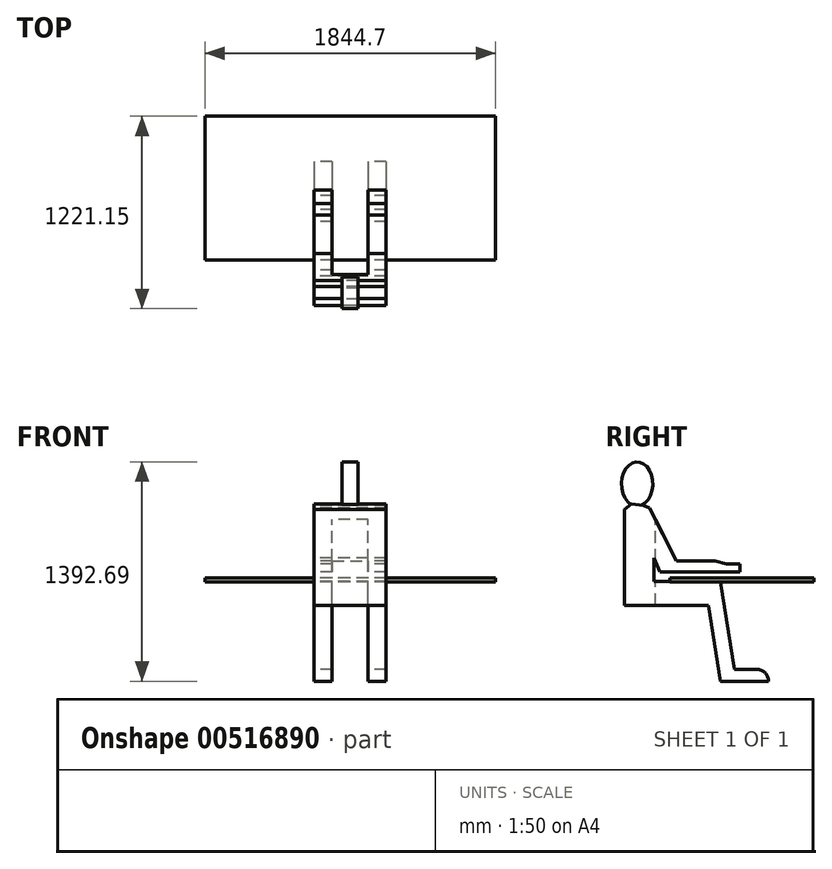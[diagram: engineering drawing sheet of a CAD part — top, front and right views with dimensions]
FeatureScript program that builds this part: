
annotation { "Feature Type Name" : "Feature", "Feature Type Description" : "" }
export const myFeature = defineFeature(function(context is Context, id is Id, definition is map)
    precondition{}
    {
        {
            var Q0;
            Q0=qCreatedBy(makeId("Right.planeOp"),FACE);
            var sketch = newSketch(context, id + "F0", { "sketchPlane" : qUnion([Q0])});
            skLineSegment(sketch, "E0", {"start": v(0, 0) * mm, "end": v(-304.8, 0) * mm});
            skLineSegment(sketch, "E1", {"start": v(-304.8, 0) * mm, "end": v(-381, 482.6) * mm});
            skArc(sketch, "E2", {"start": v(0, 0) * mm, "mid": v(-22.32, 53.88) * mm, "end": v(-76.2, 76.2) * mm});
            skLineSegment(sketch, "E3", {"start": v(-76.2, 76.2) * mm, "end": v(-216.57, 76.2) * mm});
            skLineSegment(sketch, "E4", {"start": v(-216.57, 76.2) * mm, "end": v(-304.8, 635) * mm});
            skLineSegment(sketch, "E5", {"start": v(-304.8, 635) * mm, "end": v(-728.15, 635) * mm});
            skLineSegment(sketch, "E6", {"start": v(-381, 482.6) * mm, "end": v(-914.4, 482.6) * mm});
            skLineSegment(sketch, "E7", {"start": v(-914.4, 482.6) * mm, "end": v(-914.4, 1092.2) * mm});
            skLineSegment(sketch, "E8", {"start": v(-728.15, 635) * mm, "end": v(-728.15, 784.38) * mm});
            skLineSegment(sketch, "E9", {"start": v(-728.15, 784.38) * mm, "end": v(-690.47, 694.79) * mm});
            skLineSegment(sketch, "E10", {"start": v(-690.47, 694.79) * mm, "end": v(-180.9, 694.79) * mm});
            skLineSegment(sketch, "E11", {"start": v(-180.9, 694.79) * mm, "end": v(-180.9, 744.25) * mm});
            skLineSegment(sketch, "E12", {"start": v(-180.9, 744.25) * mm, "end": v(-267.9, 744.25) * mm});
            skLineSegment(sketch, "E13", {"start": v(-267.9, 744.25) * mm, "end": v(-340.03, 765.57) * mm});
            skLineSegment(sketch, "E14", {"start": v(-340.03, 765.57) * mm, "end": v(-585.95, 765.57) * mm});
            skLineSegment(sketch, "E15", {"start": v(-585.95, 765.57) * mm, "end": v(-755.79, 1100.3) * mm});
            skLineSegment(sketch, "E16", {"start": v(-755.79, 1100.3) * mm, "end": v(-794.84, 1117.7) * mm});
            skLineSegment(sketch, "E17", {"start": v(-794.84, 1117.7) * mm, "end": v(-871.18, 1125.26) * mm});
            skLineSegment(sketch, "E18", {"start": v(-871.18, 1125.26) * mm, "end": v(-914.4, 1092.2) * mm});
            skPoint(sketch, "E19.start.orphan", {"position": v(-728.15, 1400.05) * mm});
            skSolve(sketch);
        }
        {
            var Q0;
            Q0 = qSketchRegion(id + "F0", true);
            extrude(context, id + "F1", {"entities" : qUnion([Q0]), "endBound" : BoundingType.SYMMETRIC, "depth" : 457.2 * mm, "offsetDistance" : 25.4 * mm});
        }
        {
            var Q0;
            Q0=qCreatedBy(makeId("Right.planeOp"),FACE);
            var sketch = newSketch(context, id + "F2", { "sketchPlane" : qUnion([Q0])});
            skLineSegment(sketch, "E20.bottom", {"start": v(156.03, -45.07) * mm, "end": v(-719.75, -45.07) * mm});
            skLineSegment(sketch, "E20.top", {"start": v(156.03, 1098.62) * mm, "end": v(-719.75, 1098.62) * mm});
            skLineSegment(sketch, "E20.left", {"start": v(156.03, -45.07) * mm, "end": v(156.03, 1098.62) * mm});
            skLineSegment(sketch, "E20.right", {"start": v(-719.75, -45.07) * mm, "end": v(-719.75, 1098.62) * mm});
            skSolve(sketch);
        }
        {
            var Q0;
            Q0 = qSketchRegion(id + "F2", true);
            extrude(context, id + "F3", {"entities" : qUnion([Q0]), "operationType" : NewBodyOperationType.REMOVE, "endBound" : BoundingType.SYMMETRIC, "depth" : 228.6 * mm, "offsetDistance" : 25.4 * mm});
        }
        {
            var Q0;
            Q0=qCreatedBy(makeId("Right.planeOp"),FACE);
            var sketch = newSketch(context, id + "F4", { "sketchPlane" : qUnion([Q0])});
            skEllipse(sketch, "E21", {"center": v(-834.82, 1252.77) * mm, "majorRadius": 139.92 * mm, "minorRadius": 99.98 * mm, "majorAxis": v(0, -1)});
            skSolve(sketch);
        }
        {
            var Q0;
            Q0 = qSketchRegion(id + "F4", true);
            extrude(context, id + "F5", {"entities" : qUnion([Q0]), "operationType" : NewBodyOperationType.ADD, "endBound" : BoundingType.SYMMETRIC, "depth" : 101.6 * mm, "offsetDistance" : 25.4 * mm});
        }
        {
            var Q0;
            Q0=qCreatedBy(makeId("Top.planeOp"),FACE);
            cPlane(context, id + "F6", {"entities" : qUnion([Q0]), "cplaneType" : CPlaneType.OFFSET, "offset" : 632.46 * mm, "width" : 152.4 * mm, "height" : 152.4 * mm});
        }
        {
            var Q0;
            Q0=qCreatedBy(id+"F6.planeOp",FACE);
            var sketch = newSketch(context, id + "F7", { "sketchPlane" : qUnion([Q0])});
            skLineSegment(sketch, "E22.bottom", {"start": v(922.35, 286.35) * mm, "end": v(-922.35, 286.35) * mm});
            skLineSegment(sketch, "E22.top", {"start": v(922.35, -628.05) * mm, "end": v(-922.35, -628.05) * mm});
            skLineSegment(sketch, "E22.left", {"start": v(922.35, 286.35) * mm, "end": v(922.35, -628.05) * mm});
            skLineSegment(sketch, "E22.right", {"start": v(-922.35, 286.35) * mm, "end": v(-922.35, -628.05) * mm});
            skPoint(sketch, "E22.middle", {"position": v(0, -170.85) * mm});
            skSolve(sketch);
        }
        {
            var Q0;
            Q0 = qSketchRegion(id + "F7", true);
            extrude(context, id + "F8", {"entities" : qUnion([Q0]), "depth" : 25.4 * mm, "offsetDistance" : 25.4 * mm});
        }
    });
